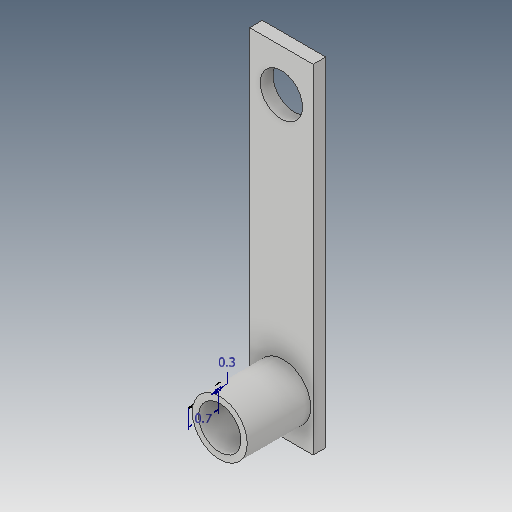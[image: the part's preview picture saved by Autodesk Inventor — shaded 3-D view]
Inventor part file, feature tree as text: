
AUTODESK INVENTOR PART (.ipt)
format: ipt  version: 2019 (Build 230136000, 136)  size: 126,464 bytes
history: native  units: in
note: dims shown in document units (in); Inventor stores cm internally (conversion verified against a paired STEP export)
features: sketch x6, extrude x4
ambient origin geometry x8: Origin, YZ Plane, XZ Plane, XY Plane, X Axis, Y Axis, Z Axis, Center Point
bodies: Solid1 (feature_tree)
feature tree (10):
  sketch  "Sketch1"  dims[d0=0.5906in d1=3.1496in]
  extrude  "Extrusion1"  Depth=3.1496in
  extrude  "Extrusion2"  Depth=0.3937in
  extrude  "Extrusion3"  Depth=0.3937in
  extrude  "Extrusion4"  Depth=0.3937in
  sketch  "Sketch6"  dims[d10=0.5118in d11=0.5906in d12=0.0in d13=0.3937in d14=0.5906in d15=0.0in d16=0.2756in d17=0.1181in]
  sketch  "Sketch2"  dims[d2=0.1181in d3=0.0in d4=0.3937in]
  sketch  "Sketch3"  dims[d5=0.3937in d6=0.3937in]
  sketch  "Sketch4"  dims[d7=0.3937in d8=0.3937in]
  sketch  "Sketch5"  dims[d9=0.0in]
